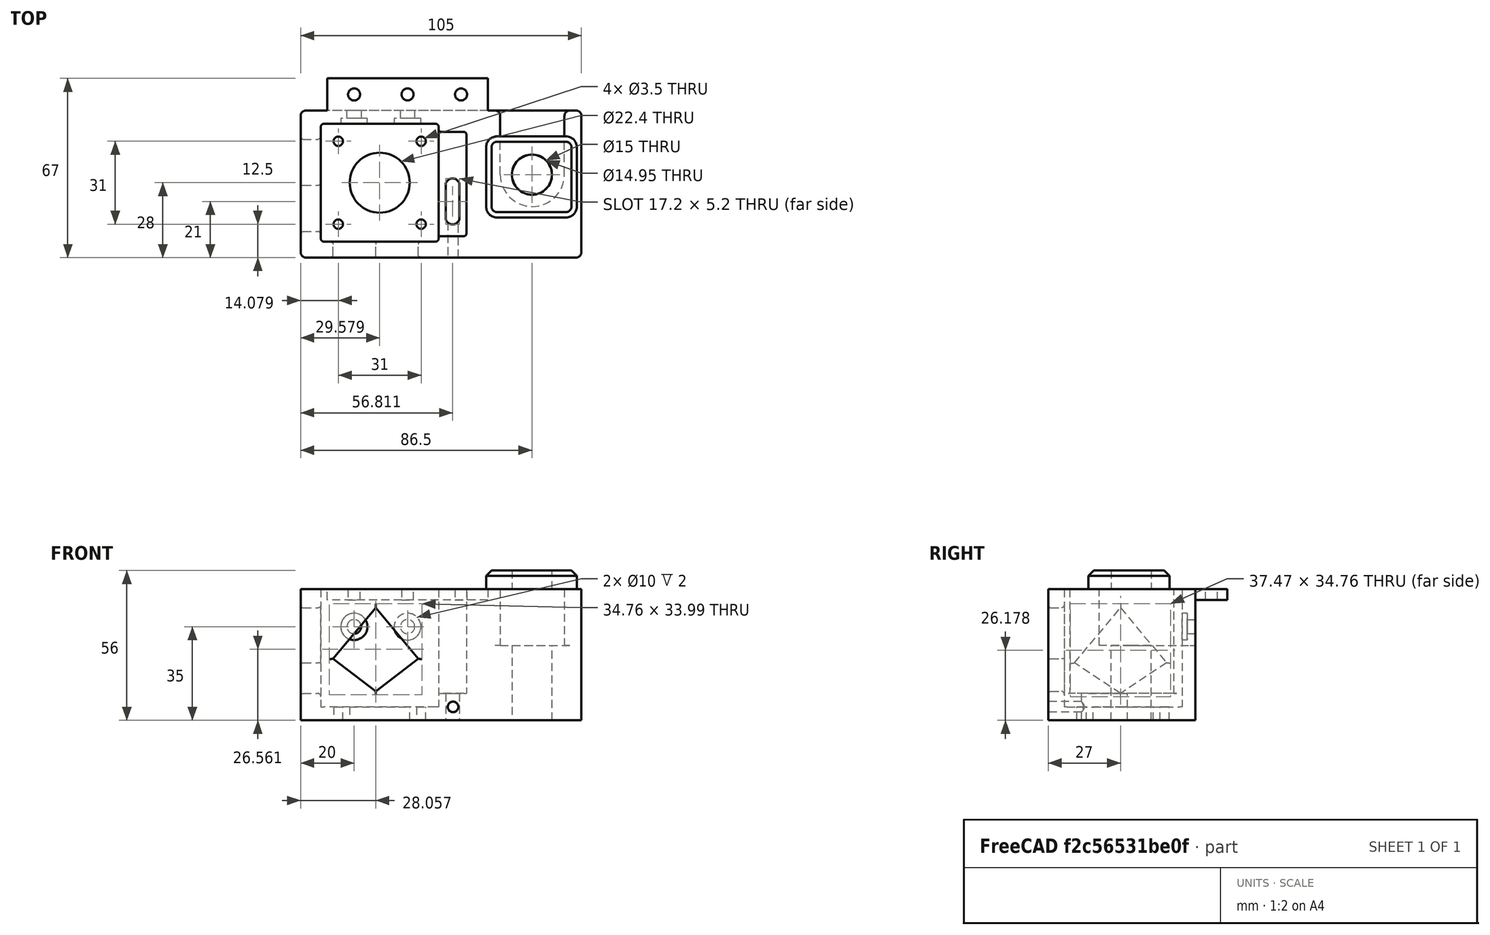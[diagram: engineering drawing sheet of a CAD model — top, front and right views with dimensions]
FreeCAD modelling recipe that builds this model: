
FCSTD DOCUMENT  (FreeCAD 0.19R)
Label: BeltY
License: All rights reserved
LicenseURL: http://en.wikipedia.org/wiki/All_rights_reserved
objects: Sketcher::SketchObject×18, PartDesign::Pocket×13, PartDesign::Fillet×9, PartDesign::Pad×3, PartDesign::Chamfer×1, PartDesign::Body×1, Mesh::Feature×1
note: 71 computed .brp shape members not serialized (recipe doc carries the construction recipe); baked Part::Feature solids carry a one-line shape summary decoded from their .brp

FEATURE [Sketcher::SketchObject] Sketch  label="body"
  FullyConstrained = false
  MapMode = 5
  Placement = pos=(0,0,0) rot=(1,0,0;1.5708rad)
  Support = -> [XZ_Plane]
  sketch-geometry (17):
    g0: LineSegment StartX=-29.9069 StartY=0 StartZ=0 EndX=30.0931 EndY=0 EndZ=0
    g1: LineSegment StartX=30.0931 StartY=0 StartZ=0 EndX=30.0931 EndY=-20 EndZ=0
    g2: LineSegment StartX=30.0931 StartY=-20 StartZ=0 EndX=-29.9069 EndY=-20 EndZ=0
    g3: LineSegment StartX=-29.9069 StartY=-20 StartZ=0 EndX=-29.9069 EndY=0 EndZ=0
    g4: LineSegment StartX=-40 StartY=4 StartZ=0 EndX=65 EndY=4 EndZ=0
    g5: LineSegment StartX=65 StartY=4 StartZ=0 EndX=65 EndY=-45 EndZ=0
    g6: LineSegment StartX=65 StartY=-45 StartZ=0 EndX=-40 EndY=-45 EndZ=0
    g7: LineSegment StartX=-40 StartY=-45 StartZ=0 EndX=-40 EndY=4 EndZ=0
    g8: LineSegment StartX=-75 StartY=12 StartZ=0 EndX=75 EndY=12 EndZ=0
    g9: LineSegment StartX=46.3903 StartY=-0.003 StartZ=0 EndX=47.5071 EndY=-0.003 EndZ=0
    g10: LineSegment StartX=47.5071 StartY=-0.003 StartZ=0 EndX=47.5071 EndY=-6.003 EndZ=0
    g11: LineSegment StartX=47.5071 StartY=-6.003 StartZ=0 EndX=46.3903 EndY=-6.003 EndZ=0
    g12: LineSegment StartX=46.3903 StartY=-6.003 StartZ=0 EndX=46.3903 EndY=-0.003 EndZ=0
    g13: LineSegment StartX=25.4514 StartY=1.58868 StartZ=0 EndX=70.4514 EndY=1.58868 EndZ=0
    g14: LineSegment StartX=70.4514 StartY=1.58868 StartZ=0 EndX=70.4514 EndY=-30.4113 EndZ=0
    g15: LineSegment StartX=70.4514 StartY=-30.4113 StartZ=0 EndX=25.4514 EndY=-30.4113 EndZ=0
    g16: LineSegment StartX=25.4514 StartY=-30.4113 StartZ=0 EndX=25.4514 EndY=1.58868 EndZ=0
  constraints (46):
    c: Coincident(g0,g1)
    c: Coincident(g1,g2)
    c: Coincident(g2,g3)
    c: Coincident(g3,g0)
    c: Horizontal(g0)
    c: Horizontal(g2)
    c: Vertical(g1)
    c: Vertical(g3)
    c: PointOnObject(g0,g-1)
    c: Distance(g1) = 20
    c: Distance(g0) = 60
    c: Coincident(g4,g5)
    c: Coincident(g5,g6)
    c: Coincident(g6,g7)
    c: Coincident(g7,g4)
    c: Horizontal(g4)
    c: Horizontal(g6)
    c: Vertical(g5)
    c: Vertical(g7)
    c: DistanceY(g4) = 4
    c: DistanceX(g4) = -40
    c: DistanceX(g4) = 65
    c: Symmetric(g8,g8,g-2)
    c: Distance(g8) = 150
    c: DistanceY(g8) = 12
    c: Coincident(g9,g10)
    c: Coincident(g10,g11)
    c: Coincident(g11,g12)
    c: Coincident(g12,g9)
    c: Horizontal(g9)
    c: Horizontal(g11)
    c: Vertical(g10)
    c: Vertical(g12)
    c: Distance(g10) = 6
    c: DistanceY(g9) = -0.003
    c: Coincident(g13,g14)
    c: Coincident(g14,g15)
    c: Coincident(g15,g16)
    c: Coincident(g16,g13)
    c: Horizontal(g13)
    c: Horizontal(g15)
    c: Vertical(g14)
    c: Vertical(g16)
    c: Distance(g14) = 32
    c: Distance(g15) = 45
    c: DistanceY(g5) = -45
FEATURE [PartDesign::Pad] Pad
  Direction = (1,1,1)
  Length = 55
  Length2 = 100
  Placement = pos=(0,0,0) rot=(1,0,0;1.5708rad)
  Profile = -> Sketch
  Type = 0
FEATURE [Sketcher::SketchObject] Sketch003  label="HOLESBOSS"
  FullyConstrained = true
  MapMode = 5
  Placement = pos=(0,0,0) rot=(-1,0,0;1.5708rad)
  Support = -> [Pad]
  sketch-geometry (4):
    g0: LineSegment StartX=-30 StartY=-4 StartZ=0 EndX=30 EndY=-4 EndZ=0
    g1: LineSegment StartX=30 StartY=-4 StartZ=0 EndX=30 EndY=0 EndZ=0
    g2: LineSegment StartX=30 StartY=0 StartZ=0 EndX=-30 EndY=0 EndZ=0
    g3: LineSegment StartX=-30 StartY=0 StartZ=0 EndX=-30 EndY=-4 EndZ=0
  constraints (12):
    c: Coincident(g0,g1)
    c: Coincident(g1,g2)
    c: Coincident(g2,g3)
    c: Coincident(g3,g0)
    c: Horizontal(g0)
    c: Horizontal(g2)
    c: Vertical(g1)
    c: Vertical(g3)
    c: DistanceX(g2) = -30
    c: DistanceX(g1) = 30
    c: PointOnObject(g2,g-1)
    c: DistanceY(g0) = -4
FEATURE [PartDesign::Pad] Pad001
  BaseFeature = -> Pad
  Direction = (1,1,1)
  Length = 12
  Length2 = 100
  Placement = pos=(0,0,0) rot=(1,0,0;1.5708rad)
  Profile = -> Sketch003
  Type = 0
FEATURE [Sketcher::SketchObject] Sketch004  label="topMountHoles"
  FullyConstrained = true
  MapMode = 5
  Placement = pos=(0,-1e-15,4) rot=(0,0,1;3.14159rad)
  sketch-geometry (3):
    g0: Circle CenterX=-20 CenterY=-6 CenterZ=0 NormalX=0 NormalY=0 NormalZ=1 AngleXU=0 Radius=2.25
    g1: Circle CenterX=0 CenterY=-6 CenterZ=0 NormalX=0 NormalY=0 NormalZ=1 AngleXU=0 Radius=2.25
    g2: Circle CenterX=20 CenterY=-6 CenterZ=0 NormalX=0 NormalY=0 NormalZ=1 AngleXU=0 Radius=2.25
  constraints (8):
    c: Symmetric(g2,g0,g-2)
    c: Diameter(g2) = 4.5
    c: Equal(g2,g0)
    c: Equal(g2,g1)
    c: PointOnObject(g1,g-2)
    c: Distance(g1,g0) = 20
    c: DistanceY(g1) = -6
    c: DistanceY(g0) = -6
FEATURE [Sketcher::SketchObject] Sketch006  label="reference"
  FullyConstrained = false
  MapMode = 5
  Placement = pos=(45,0,0) rot=(0.707107,0,0.707107;3.14159rad)
  sketch-geometry (9):
    g0: LineSegment StartX=-15.7453 StartY=27.0334 StartZ=0 EndX=0.254731 EndY=27.0334 EndZ=0
    g1: LineSegment StartX=0.254731 StartY=27.0334 StartZ=0 EndX=0.254731 EndY=12.0334 EndZ=0
    g2: LineSegment StartX=0.254731 StartY=12.0334 StartZ=0 EndX=-15.7453 EndY=12.0334 EndZ=0
    g3: LineSegment StartX=-15.7453 StartY=12.0334 StartZ=0 EndX=-15.7453 EndY=27.0334 EndZ=0
    g4: LineSegment StartX=-46.7453 StartY=46 StartZ=0 EndX=-30.7453 EndY=46 EndZ=0
    g5: LineSegment StartX=-30.7453 StartY=46 StartZ=0 EndX=-30.7453 EndY=1 EndZ=0
    g6: LineSegment StartX=-30.7453 StartY=1 StartZ=0 EndX=-46.7453 EndY=1 EndZ=0
    g7: LineSegment StartX=-46.7453 StartY=1 StartZ=0 EndX=-46.7453 EndY=46 EndZ=0
    g8: LineSegment StartX=-60 StartY=75.2004 StartZ=0 EndX=-60 EndY=-15.1549 EndZ=0
  constraints (24):
    c: Coincident(g0,g1)
    c: Coincident(g1,g2)
    c: Coincident(g2,g3)
    c: Coincident(g3,g0)
    c: Horizontal(g0)
    c: Horizontal(g2)
    c: Vertical(g1)
    c: Vertical(g3)
    c: Distance(g0) = 16
    c: Distance(g1) = 15
    c: Coincident(g4,g5)
    c: Coincident(g5,g6)
    c: Coincident(g6,g7)
    c: Coincident(g7,g4)
    c: Horizontal(g4)
    c: Horizontal(g6)
    c: Vertical(g5)
    c: Vertical(g7)
    c: Distance(g5) = 45
    c: Distance(g4) = 16
    c: DistanceY(g5) = 1
    c: Distance(g2,g5) = 15
    c: Vertical(g8)
    c: DistanceX(g8) = -60
FEATURE [Sketcher::SketchObject] Sketch009  label="6mmBearing"
  ExternalGeometry = -> [Pad001]
  FullyConstrained = false
  MapMode = 5
  Placement = pos=(0,9e-16,4) rot=(0,0,1;3.14159rad)
  Support = -> [Pad001]
  sketch-geometry (3):
    g0: Circle CenterX=-46.5 CenterY=24 CenterZ=0 NormalX=0 NormalY=0 NormalZ=1 AngleXU=0 Radius=7.475
    g1: Circle CenterX=-46.5 CenterY=24 CenterZ=0 NormalX=0 NormalY=0 NormalZ=1 AngleXU=0 Radius=22.5
    g2: Circle CenterX=-46.5 CenterY=24 CenterZ=0 NormalX=0 NormalY=0 NormalZ=1 AngleXU=0 Radius=2.14458
  constraints (5):
    c: Diameter(g0) = 14.95
    c: Coincident(g1,g0)
    c: Coincident(g2,g0)
    c: Diameter(g1) = 45
    c: DistanceX(g0,g-3) = 16.5
FEATURE [PartDesign::Pocket] Pocket
  BaseFeature = -> Pad001
  Length = 5
  Length2 = 100
  Placement = pos=(0,0,0) rot=(1,0,0;1.5708rad)
  Profile = -> Sketch009
  Type = 1
FEATURE [Sketcher::SketchObject] Sketch007  label="BeltPath"
  ExternalGeometry = -> [Pocket]
  FullyConstrained = false
  MapMode = 5
  Placement = pos=(0,9e-16,4) rot=(0,0,1;3.14159rad)
  Support = -> [Pocket]
  sketch-geometry (4):
    g0: ArcOfCircle CenterX=-46.6565 CenterY=23.899 CenterZ=0 NormalX=0 NormalY=0 NormalZ=1 AngleXU=0 Radius=12 StartAngle=0 EndAngle=3.14159
    g1: LineSegment StartX=-58.6565 StartY=23.899 StartZ=0 EndX=-58.6565 EndY=-0.01 EndZ=0
    g2: LineSegment StartX=-34.6565 StartY=23.899 StartZ=0 EndX=-34.6565 EndY=-0.01 EndZ=0
    g3: LineSegment StartX=-58.6565 StartY=-0.01 StartZ=0 EndX=-34.6565 EndY=-0.01 EndZ=0
  constraints (9):
    c: Vertical(g1)
    c: Vertical(g2)
    c: Tangent(g1,g0) = -1.5708
    c: Tangent(g2,g0) = 1.5708
    c: Diameter(g0) = 24
    c: Coincident(g3,g2)
    c: Coincident(g3,g1)
    c: DistanceY(g1) = -0.01
    c: DistanceY(g2) = -0.01
FEATURE [PartDesign::Pocket] Pocket001
  BaseFeature = -> Pocket
  Length = 21
  Length2 = 100
  Placement = pos=(0,0,0) rot=(1,0,0;1.5708rad)
  Profile = -> Sketch007
  Type = 0
FEATURE [Sketcher::SketchObject] Sketch002  label="StepperHoles"
  ExternalGeometry = -> [Pocket001]
  FullyConstrained = true
  MapMode = 5
  Placement = pos=(0,9e-16,4) rot=(0,0,1;3.14159rad)
  Support = -> [Pocket001]
  sketch-geometry (11):
    g0: Circle CenterX=-5.079 CenterY=42.5 CenterZ=0 NormalX=0 NormalY=0 NormalZ=1 AngleXU=0 Radius=1.75
    g1: Circle CenterX=25.921 CenterY=42.5 CenterZ=0 NormalX=0 NormalY=0 NormalZ=1 AngleXU=0 Radius=1.75
    g2: Circle CenterX=-5.079 CenterY=11.5 CenterZ=0 NormalX=0 NormalY=0 NormalZ=1 AngleXU=0 Radius=1.75
    g3: Circle CenterX=25.921 CenterY=11.5 CenterZ=0 NormalX=0 NormalY=0 NormalZ=1 AngleXU=0 Radius=1.75
    g4: Circle CenterX=10.421 CenterY=27 CenterZ=0 NormalX=0 NormalY=0 NormalZ=1 AngleXU=0 Radius=11.2
    g5: LineSegment StartX=25.921 StartY=42.5 StartZ=0 EndX=-5.079 EndY=42.5 EndZ=0
    g6: LineSegment StartX=-5.079 StartY=42.5 StartZ=0 EndX=-5.079 EndY=11.5 EndZ=0
    g7: LineSegment StartX=-10.579 StartY=48 StartZ=0 EndX=31.421 EndY=48 EndZ=0
    g8: LineSegment StartX=31.421 StartY=48 StartZ=0 EndX=31.421 EndY=6 EndZ=0
    g9: LineSegment StartX=31.421 StartY=6 StartZ=0 EndX=-10.579 EndY=6 EndZ=0
    g10: LineSegment StartX=-10.579 StartY=6 StartZ=0 EndX=-10.579 EndY=48 EndZ=0
  constraints (28):
    c: Diameter(g1) = 3.5
    c: Equal(g1,g0)
    c: Equal(g1,g2)
    c: Equal(g1,g3)
    c: Distance(g0,g1) = 31
    c: Distance(g2,g0) = 31
    c: Symmetric(g1,g2,g4)
    c: Symmetric(g0,g3,g4)
    c: Coincident(g5,g1)
    c: Coincident(g5,g0)
    c: Horizontal(g5)
    c: Diameter(g4) = 22.4
    c: Coincident(g6,g0)
    c: Coincident(g6,g2)
    c: Vertical(g6)
    c: Coincident(g7,g8)
    c: Coincident(g8,g9)
    c: Coincident(g9,g10)
    c: Coincident(g10,g7)
    c: Horizontal(g7)
    c: Horizontal(g9)
    c: Vertical(g8)
    c: Vertical(g10)
    c: Distance(g8) = 42
    c: Equal(g9,g8)
    c: Symmetric(g8,g7,g4)
    c: DistanceY(g4) = 27
    c: Distance(g4,g-4) = 57
FEATURE [PartDesign::Pocket] Pocket002
  BaseFeature = -> Pocket001
  Length = 5
  Length2 = 100
  Placement = pos=(0,0,0) rot=(1,0,0;1.5708rad)
  Profile = -> Sketch002
  Type = 1
FEATURE [Sketcher::SketchObject] Sketch008  label="StepperWell"
  ExternalGeometry = -> [Pocket002]
  FullyConstrained = true
  MapMode = 5
  Placement = pos=(0,1.3e-15,4) rot=(0,0,1;3.14159rad)
  Support = -> [Pocket002]
  sketch-geometry (4):
    g0: LineSegment StartX=-11.579 StartY=49 StartZ=0 EndX=32.421 EndY=49 EndZ=0
    g1: LineSegment StartX=32.421 StartY=49 StartZ=0 EndX=32.421 EndY=5 EndZ=0
    g2: LineSegment StartX=32.421 StartY=5 StartZ=0 EndX=-11.579 EndY=5 EndZ=0
    g3: LineSegment StartX=-11.579 StartY=5 StartZ=0 EndX=-11.579 EndY=49 EndZ=0
  constraints (11):
    c: Coincident(g0,g1)
    c: Coincident(g1,g2)
    c: Horizontal(g0)
    c: Horizontal(g2)
    c: Vertical(g1)
    c: Coincident(g2,g3)
    c: Vertical(g3)
    c: Distance(g2) = 44
    c: Distance(g1) = 44
    c: Coincident(g3,g0)
    c: Symmetric(g0,g2,g-3)
FEATURE [Sketcher::SketchObject] Sketch013  label="SideMountHoles"
  FullyConstrained = true
  MapMode = 5
  Placement = pos=(0,0,0) rot=(-1,0,0;1.5708rad)
  sketch-geometry (2):
    g0: Circle CenterX=0 CenterY=10 CenterZ=0 NormalX=0 NormalY=0 NormalZ=1 AngleXU=0 Radius=2.65
    g1: Circle CenterX=-20 CenterY=10 CenterZ=0 NormalX=0 NormalY=0 NormalZ=1 AngleXU=0 Radius=2.65
  constraints (6):
    c: Diameter(g1) = 5.3
    c: Equal(g1,g0)
    c: PointOnObject(g0,g-2)
    c: DistanceY(g0) = 10
    c: DistanceX(g1) = -20
    c: DistanceY(g1) = 10
FEATURE [Sketcher::SketchObject] Sketch016  label="JackScrew"
  FullyConstrained = true
  MapMode = 5
  Placement = pos=(0,-55,-1.2e-14) rot=(1,0,0;1.5708rad)
  sketch-geometry (1):
    g0: Circle CenterX=17 CenterY=-40 CenterZ=0 NormalX=0 NormalY=0 NormalZ=1 AngleXU=0 Radius=1.975
  constraints (3):
    c: Diameter(g0) = 3.95
    c: DistanceY(g0) = -40
    c: DistanceX(g0) = 17
FEATURE [Sketcher::SketchObject] Sketch018
  FullyConstrained = true
  MapMode = 5
  Placement = pos=(0,-55,-1.2e-14) rot=(1,0,0;1.5708rad)
  sketch-geometry (4):
    g0: LineSegment StartX=-11.9429 StartY=-3 StartZ=0 EndX=-27.8858 EndY=-22 EndZ=0
    g1: LineSegment StartX=-27.8858 StartY=-22 StartZ=0 EndX=-11.9429 EndY=-34.1749 EndZ=0
    g2: LineSegment StartX=-11.9429 StartY=-34.1749 StartZ=0 EndX=4 EndY=-22 EndZ=0
    g3: LineSegment StartX=4 StartY=-22 StartZ=0 EndX=-11.9429 EndY=-3 EndZ=0
  constraints (12):
    c: Coincident(g0,g1)
    c: Coincident(g1,g2)
    c: Coincident(g2,g3)
    c: Coincident(g3,g0)
    c: Angle(g0,g3) = 1.39626
    c: Equal(g3,g0)
    c: DistanceY(g0) = -22
    c: DistanceY(g2) = -22
    c: DistanceY(g0) = -3
    c: Equal(g1,g2)
    c: Distance(g2) = 20.06
    c: DistanceX(g2) = 4
FEATURE [Sketcher::SketchObject] Sketch019
  FullyConstrained = false
  MapMode = 5
  Placement = pos=(0,-33.5,-7.4e-15) rot=(-1,0,0;1.5708rad)
  sketch-geometry (3):
    g0: LineSegment StartX=25.4858 StartY=0 StartZ=0 EndX=25.4858 EndY=20 EndZ=0
    g1: LineSegment StartX=29.1276 StartY=14 StartZ=0 EndX=29.1276 EndY=2 EndZ=0
    g2: LineSegment StartX=29.1276 StartY=17 StartZ=0 EndX=29.1276 EndY=14 EndZ=0
  constraints (9):
    c: PointOnObject(g0,g-1)
    c: Vertical(g0)
    c: Distance(g0) = 20
    c: Vertical(g1)
    c: Distance(g1) = 12
    c: DistanceY(g1,g0) = 6
    c: Vertical(g2)
    c: Distance(g2) = 3
    c: Coincident(g2,g1)
FEATURE [PartDesign::Pocket] Pocket003
  BaseFeature = -> Pocket002
  Length = 44
  Length2 = 100
  Placement = pos=(0,0,0) rot=(1,0,0;1.5708rad)
  Profile = -> Sketch008
  Type = 0
FEATURE [Sketcher::SketchObject] Sketch011  label="SlotWell"
  FullyConstrained = true
  MapMode = 5
  Placement = pos=(0,1.8e-15,4) rot=(0,0,1;3.14159rad)
  Support = -> [Pocket003]
  sketch-geometry (4):
    g0: LineSegment StartX=-22 StartY=47 StartZ=0 EndX=-4.3 EndY=47 EndZ=0
    g1: LineSegment StartX=-4.3 StartY=47 StartZ=0 EndX=-4.3 EndY=8 EndZ=0
    g2: LineSegment StartX=-4.3 StartY=8 StartZ=0 EndX=-22 EndY=8 EndZ=0
    g3: LineSegment StartX=-22 StartY=8 StartZ=0 EndX=-22 EndY=47 EndZ=0
  constraints (12):
    c: Coincident(g0,g1)
    c: Coincident(g1,g2)
    c: Coincident(g2,g3)
    c: Coincident(g3,g0)
    c: Horizontal(g0)
    c: Horizontal(g2)
    c: Vertical(g1)
    c: Vertical(g3)
    c: DistanceX(g2) = -22
    c: DistanceY(g0) = 47
    c: DistanceX(g1) = -4.3
    c: DistanceY(g2) = 8
FEATURE [PartDesign::Pocket] Pocket004
  BaseFeature = -> Pocket003
  Length = 39
  Length2 = 100
  Placement = pos=(0,0,0) rot=(1,0,0;1.5708rad)
  Profile = -> Sketch011
  Type = 0
FEATURE [Sketcher::SketchObject] Sketch012  label="Slot"
  FullyConstrained = false
  MapMode = 5
  Placement = pos=(0,-1.98e-14,-35) rot=(0,0,1;3.14159rad)
  Support = -> [Pocket004]
  sketch-geometry (4):
    g0: ArcOfCircle CenterX=-16.8114 CenterY=40 CenterZ=0 NormalX=0 NormalY=0 NormalZ=1 AngleXU=0 Radius=2.6 StartAngle=0 EndAngle=3.14159
    g1: ArcOfCircle CenterX=-16.8114 CenterY=28 CenterZ=0 NormalX=0 NormalY=0 NormalZ=1 AngleXU=0 Radius=2.6 StartAngle=3.14159 EndAngle=6.28319
    g2: LineSegment StartX=-19.4114 StartY=40 StartZ=0 EndX=-19.4114 EndY=28 EndZ=0
    g3: LineSegment StartX=-14.2114 StartY=40 StartZ=0 EndX=-14.2114 EndY=28 EndZ=0
  constraints (9):
    c: Tangent(g0,g3) = 1.5708
    c: Tangent(g0,g2) = -1.5708
    c: Tangent(g2,g1) = -1.5708
    c: Tangent(g3,g1) = 1.5708
    c: Vertical(g2)
    c: Equal(g0,g1)
    c: Distance(g1,g1) = 5.2
    c: Distance(g1,g0) = 12
    c: DistanceY(g1) = 28
FEATURE [PartDesign::Pocket] Pocket005
  BaseFeature = -> Pocket004
  Length = 5
  Length2 = 100
  Placement = pos=(0,0,0) rot=(1,0,0;1.5708rad)
  Profile = -> Sketch012
  Type = 1
FEATURE [PartDesign::Pocket] Pocket006
  BaseFeature = -> Pocket005
  Length = 14
  Length2 = 100
  Placement = pos=(0,0,0) rot=(1,0,0;1.5708rad)
  Profile = -> Sketch013
  Type = 0
FEATURE [Sketcher::SketchObject] Sketch015  label="SideCountersink"
  FullyConstrained = false
  MapMode = 5
  Placement = pos=(0,-5,3.9e-15) rot=(1,0,0;1.5708rad)
  Support = -> [Pocket006]
  sketch-geometry (2):
    g0: Circle CenterX=-20 CenterY=-10 CenterZ=0 NormalX=0 NormalY=0 NormalZ=1 AngleXU=0 Radius=5
    g1: Circle CenterX=0 CenterY=-10 CenterZ=0 NormalX=0 NormalY=0 NormalZ=1 AngleXU=0 Radius=5
  constraints (2):
    c: Diameter(g1) = 10
    c: Equal(g1,g0)
FEATURE [PartDesign::Pocket] Pocket007
  BaseFeature = -> Pocket006
  Length = 2
  Length2 = 100
  Placement = pos=(0,0,0) rot=(1,0,0;1.5708rad)
  Profile = -> Sketch015
  Type = 0
FEATURE [PartDesign::Pocket] Pocket008
  BaseFeature = -> Pocket007
  Length = 23
  Length2 = 100
  Placement = pos=(0,0,0) rot=(1,0,0;1.5708rad)
  Profile = -> Sketch016
  Type = 0
FEATURE [PartDesign::Pocket] Pocket009
  BaseFeature = -> Pocket008
  Length = 5
  Length2 = 100
  Placement = pos=(0,0,0) rot=(1,0,0;1.5708rad)
  Profile = -> Sketch004
  Type = 0
FEATURE [PartDesign::Pocket] Pocket010
  BaseFeature = -> Pocket009
  Length = 9
  Length2 = 100
  Placement = pos=(0,0,0) rot=(1,0,0;1.5708rad)
  Profile = -> Sketch018
  Type = 0
FEATURE [Sketcher::SketchObject] Sketch017  label="SideCooling"
  FullyConstrained = true
  MapMode = 5
  Placement = pos=(-40,0,0) rot=(0.707107,0,-0.707107;3.14159rad)
  Support = -> [Pocket010]
  sketch-geometry (4):
    g0: LineSegment StartX=3 StartY=28 StartZ=0 EndX=23.5581 EndY=45.2503 EndZ=0
    g1: LineSegment StartX=23.5581 StartY=45.2503 StartZ=0 EndX=35 EndY=28 EndZ=0
    g2: LineSegment StartX=35 StartY=28 StartZ=0 EndX=23.5581 EndY=10.7497 EndZ=0
    g3: LineSegment StartX=23.5581 StartY=10.7497 StartZ=0 EndX=3 EndY=28 EndZ=0
  constraints (12):
    c: Coincident(g0,g1)
    c: Coincident(g1,g2)
    c: Coincident(g2,g3)
    c: Coincident(g3,g0)
    c: Equal(g3,g0)
    c: Equal(g2,g1)
    c: DistanceY(g1) = 28
    c: Angle(g3,g0) = 1.39626
    c: DistanceX(g1) = 35
    c: DistanceX(g0) = 3
    c: Distance(g1) = 20.7
    c: DistanceY(g0) = 28
FEATURE [PartDesign::Pocket] Pocket011
  BaseFeature = -> Pocket010
  Length = 8
  Length2 = 100
  Placement = pos=(0,0,0) rot=(1,0,0;1.5708rad)
  Profile = -> Sketch017
  Type = 0
FEATURE [Sketcher::SketchObject] Sketch020
  FullyConstrained = false
  MapMode = 5
  Placement = pos=(0,5.3e-15,4) rot=(0,0,1;3.14159rad)
  Support = -> [Pocket011]
  sketch-geometry (4):
    g0: LineSegment StartX=-63.2697 StartY=39.9881 StartZ=0 EndX=-29.3775 EndY=39.9881 EndZ=0
    g1: LineSegment StartX=-29.3775 StartY=39.9881 StartZ=0 EndX=-29.3775 EndY=9.69219 EndZ=0
    g2: LineSegment StartX=-29.3775 StartY=9.69219 StartZ=0 EndX=-63.2697 EndY=9.69219 EndZ=0
    g3: LineSegment StartX=-63.2697 StartY=9.69219 StartZ=0 EndX=-63.2697 EndY=39.9881 EndZ=0
  constraints (8):
    c: Coincident(g0,g1)
    c: Coincident(g1,g2)
    c: Coincident(g2,g3)
    c: Coincident(g3,g0)
    c: Horizontal(g0)
    c: Horizontal(g2)
    c: Vertical(g1)
    c: Vertical(g3)
FEATURE [PartDesign::Pad] Pad002
  BaseFeature = -> Pocket011
  Direction = (1,1,1)
  Length = 7
  Length2 = 100
  Placement = pos=(0,0,0) rot=(1,0,0;1.5708rad)
  Profile = -> Sketch020
  Type = 0
FEATURE [Sketcher::SketchObject] Sketch021
  ExternalGeometry = -> [Pad002]
  FullyConstrained = true
  MapMode = 5
  Placement = pos=(0,5.7e-15,4) rot=(1,0,0;3.14159rad)
  Support = -> [Pad002]
  sketch-geometry (1):
    g0: Circle CenterX=46.5 CenterY=24 CenterZ=0 NormalX=0 NormalY=0 NormalZ=1 AngleXU=0 Radius=7.5
  constraints (2):
    c: Radius(g0) = 7.5
    c: Coincident(g0,g-3)
FEATURE [PartDesign::Pocket] Pocket012
  BaseFeature = -> Pad002
  Length = 5
  Length2 = 100
  Placement = pos=(0,0,0) rot=(1,0,0;1.5708rad)
  Profile = -> Sketch021
  Type = 1
FEATURE [PartDesign::Fillet] Fillet
  Base = -> Pocket012 [Edge44,Edge43,Edge47,Edge49]
  BaseFeature = -> Pocket012
  Placement = pos=(0,0,0) rot=(1,0,0;1.5708rad)
  Radius = 4
  SupportTransform = false
FEATURE [PartDesign::Fillet] Fillet001
  Base = -> Fillet [Edge40,Edge42,Edge34,Edge41,Edge62,Edge69]
  BaseFeature = -> Fillet
  Placement = pos=(0,0,0) rot=(1,0,0;1.5708rad)
  Radius = 2
  SupportTransform = false
FEATURE [PartDesign::Fillet] Fillet002
  Base = -> Fillet001 [Edge124,Edge115,Edge112,Edge122,Edge106,Edge101]
  BaseFeature = -> Fillet001
  Placement = pos=(0,0,0) rot=(1,0,0;1.5708rad)
  Radius = 1
  SupportTransform = false
FEATURE [PartDesign::Fillet] Fillet003
  Base = -> Fillet002 [Edge51]
  BaseFeature = -> Fillet002
  Placement = pos=(0,0,0) rot=(1,0,0;1.5708rad)
  Radius = 0.5
  SupportTransform = false
FEATURE [PartDesign::Fillet] Fillet004
  Base = -> Fillet003 [Edge45]
  BaseFeature = -> Fillet003
  Placement = pos=(0,0,0) rot=(1,0,0;1.5708rad)
  Radius = 1
  SupportTransform = false
FEATURE [PartDesign::Fillet] Fillet005
  Base = -> Fillet004 [Edge128,Edge127,Edge126,Edge125]
  BaseFeature = -> Fillet004
  Placement = pos=(0,0,0) rot=(1,0,0;1.5708rad)
  Radius = 1
  SupportTransform = false
FEATURE [PartDesign::Fillet] Fillet006
  Base = -> Fillet005 [Edge99,Edge100,Edge98,Edge97]
  BaseFeature = -> Fillet005
  Placement = pos=(0,0,0) rot=(1,0,0;1.5708rad)
  Radius = 1
  SupportTransform = false
FEATURE [PartDesign::Chamfer] Chamfer
  Angle = 45
  Base = -> Fillet006 [Edge134]
  BaseFeature = -> Fillet006
  ChamferType = 0
  FlipDirection = false
  Placement = pos=(0,0,0) rot=(1,0,0;1.5708rad)
  Size = 2
  Size2 = 1
  SupportTransform = false
FEATURE [PartDesign::Fillet] Fillet007
  Base = -> Chamfer [Edge100,Edge99,Edge98,Edge101]
  BaseFeature = -> Chamfer
  Placement = pos=(0,0,0) rot=(1,0,0;1.5708rad)
  Radius = 1
  SupportTransform = false
FEATURE [PartDesign::Fillet] Fillet008
  Base = -> Fillet007 [Edge90,Edge91,Edge92,Edge89]
  BaseFeature = -> Fillet007
  Placement = pos=(0,0,0) rot=(1,0,0;1.5708rad)
  Radius = 1
  SupportTransform = false
FEATURE [PartDesign::Body] Body
  Group = -> [Sketch,Pad,Sketch002,Sketch003,Pad001,Sketch004,Sketch006,Sketch007,Sketch008,Sketch009,Pocket,Pocket001,Pocket002,Sketch011,Sketch012,Sketch013,Sketch015,Sketch016,Sketch017,Sketch018,Sketch019,Pocket003,Pocket004,Pocket005,Pocket006,Pocket007,Pocket008,Pocket009,Pocket010,Pocket011,Sketch020,Pad002,Sketch021,Pocket012,Fillet,Fillet001,Fillet002,Fillet003,Fillet004,Fillet005,Fillet006,Chamfer,+2 more]
  Origin = -> Origin
  Tip = -> Fillet008
FEATURE [Mesh::Feature] Mesh  label="Fillet008 (Meshed)"
